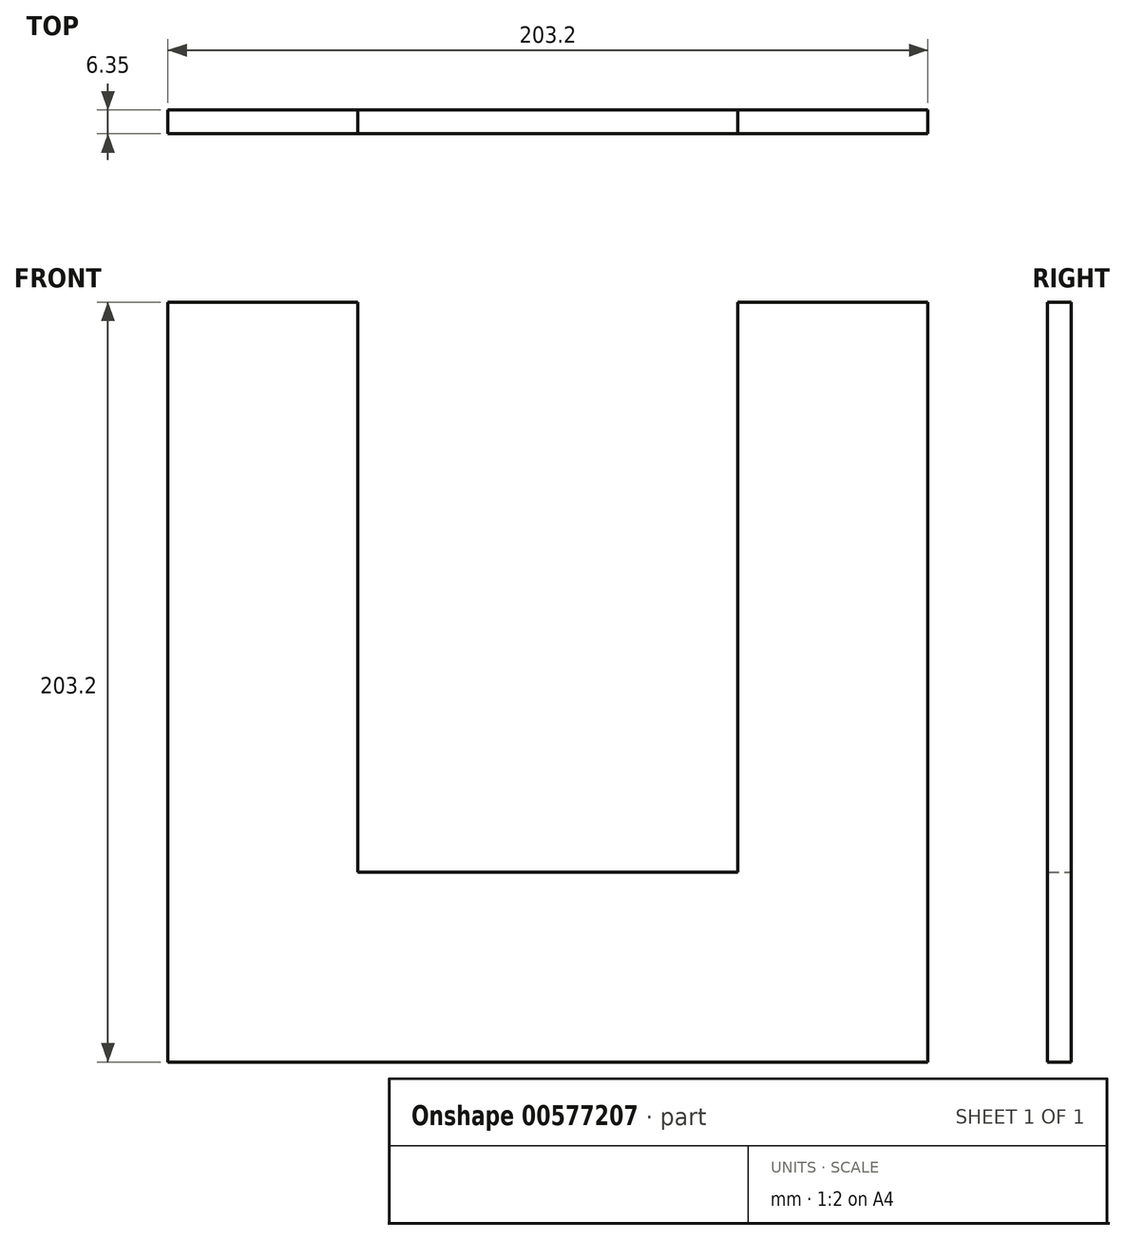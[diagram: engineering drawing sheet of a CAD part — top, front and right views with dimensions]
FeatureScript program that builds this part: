
annotation { "Feature Type Name" : "Feature", "Feature Type Description" : "" }
export const myFeature = defineFeature(function(context is Context, id is Id, definition is map)
    precondition{}
    {
        {
            var Q0;
            Q0=qCreatedBy(makeId("Front.planeOp"),FACE);
            var sketch = newSketch(context, id + "F0", { "sketchPlane" : qUnion([Q0])});
            skLineSegment(sketch, "E0", {"start": v(0, 0) * mm, "end": v(0, 203.2) * mm});
            skLineSegment(sketch, "E1", {"start": v(0, 203.2) * mm, "end": v(50.8, 203.2) * mm});
            skLineSegment(sketch, "E2", {"start": v(50.8, 203.2) * mm, "end": v(50.8, 50.8) * mm});
            skLineSegment(sketch, "E3", {"start": v(50.8, 50.8) * mm, "end": v(152.4, 50.8) * mm});
            skLineSegment(sketch, "E4", {"start": v(152.4, 50.8) * mm, "end": v(152.4, 203.2) * mm});
            skLineSegment(sketch, "E5", {"start": v(152.4, 203.2) * mm, "end": v(203.2, 203.2) * mm});
            skLineSegment(sketch, "E6", {"start": v(203.2, 203.2) * mm, "end": v(203.2, 0) * mm});
            skLineSegment(sketch, "E7", {"start": v(203.2, 0) * mm, "end": v(0, 0) * mm});
            skSolve(sketch);
        }
        {
            var Q0;
            Q0 = qSketchRegion(id + "F0", true);
            extrude(context, id + "F1", {"entities" : qUnion([Q0]), "depth" : 6.35 * mm, "offsetDistance" : 25.4 * mm});
        }
    });
